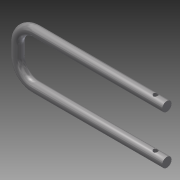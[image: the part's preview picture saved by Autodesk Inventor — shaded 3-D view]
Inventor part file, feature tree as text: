
AUTODESK INVENTOR PART (.ipt)
format: ipt  version: 2015 (Build 190159000, 159)  size: 136,192 bytes
history: native  units: mm
features: sketch x3, sweep x1, extrude x1
ambient origin geometry x8: Origin, YZ Plane, XZ Plane, XY Plane, X Axis, Y Axis, Z Axis, Center Point
bodies: Solid1 (feature_tree)
feature tree (5):
  sweep  "Sweep1"
  extrude  "Extrusion1"  Depth=50.0mm
  sketch  "Sketch1"  dims[d7=400.0mm d8=130.0mm]
  sketch  "Sketch2"  dims[d9=400.0mm d10=50.0mm]
  sketch  "Sketch3"  dims[d11=25.4mm d12=0.0mm d13=0.0mm d14=30.0mm d15=12.0mm d16=10.0mm d17=0.0mm]
